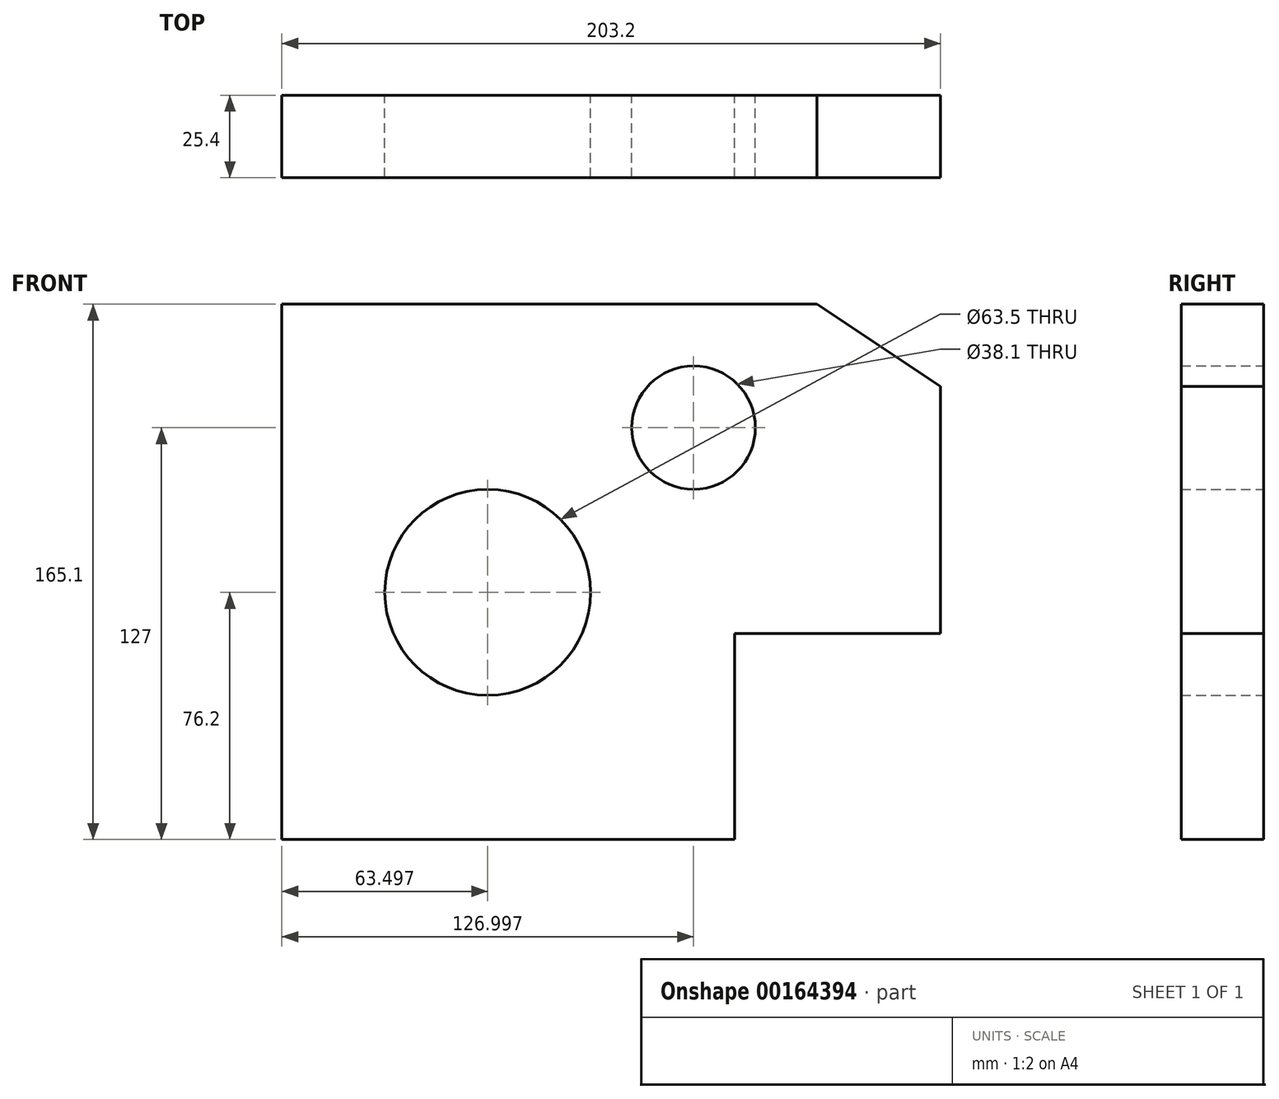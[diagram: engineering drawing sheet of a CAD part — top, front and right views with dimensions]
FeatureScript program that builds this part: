
annotation { "Feature Type Name" : "Feature", "Feature Type Description" : "" }
export const myFeature = defineFeature(function(context is Context, id is Id, definition is map)
    precondition{}
    {
        {
            var Q0;
            Q0=qCreatedBy(makeId("Front.planeOp"),FACE);
            var sketch = newSketch(context, id + "F0", { "sketchPlane" : qUnion([Q0])});
            skPoint(sketch, "E0.middle", {"position": v(-38.82, 55.06) * mm});
            skLineSegment(sketch, "E1.top", {"start": v(80.36, -12.7) * mm, "end": v(16.86, -12.7) * mm});
            skLineSegment(sketch, "E1.right", {"start": v(16.86, -76.2) * mm, "end": v(16.86, -12.7) * mm});
            skPoint(sketch, "E1.middle", {"position": v(48.6, -44.45) * mm});
            skLineSegment(sketch, "E2", {"start": v(16.86, -76.2) * mm, "end": v(-122.84, -76.2) * mm});
            skLineSegment(sketch, "E3", {"start": v(-122.84, -76.2) * mm, "end": v(-122.84, 88.9) * mm});
            skLineSegment(sketch, "E4", {"start": v(80.36, -12.7) * mm, "end": v(80.36, 63.5) * mm});
            skLineSegment(sketch, "E5", {"start": v(-122.84, 88.9) * mm, "end": v(42.26, 88.9) * mm});
            skLineSegment(sketch, "E6", {"start": v(42.26, 88.9) * mm, "end": v(80.36, 63.5) * mm});
            skCircle(sketch, "E7", {"center": v(-59.34, 0) * mm, "radius": 31.75 * mm});
            skCircle(sketch, "E8", {"center": v(4.16, 50.8) * mm, "radius": 19.05 * mm});
            skSolve(sketch);
        }
        {
            var Q0;
            Q0=makeQuery(id+"F0.imprint","IMPRINT",FACE,{"disambiguationData":[TD([[makeQuery(id+"F0.imprint","IMPRINT",EDGE,{"derivedFrom":sQuery(id+"F0.wireOp",EDGE,"E1.top")}),-1.0]])]});
            extrude(context, id + "F1", {"entities" : qUnion([Q0]), "depth" : 25.4 * mm});
        }
    });
